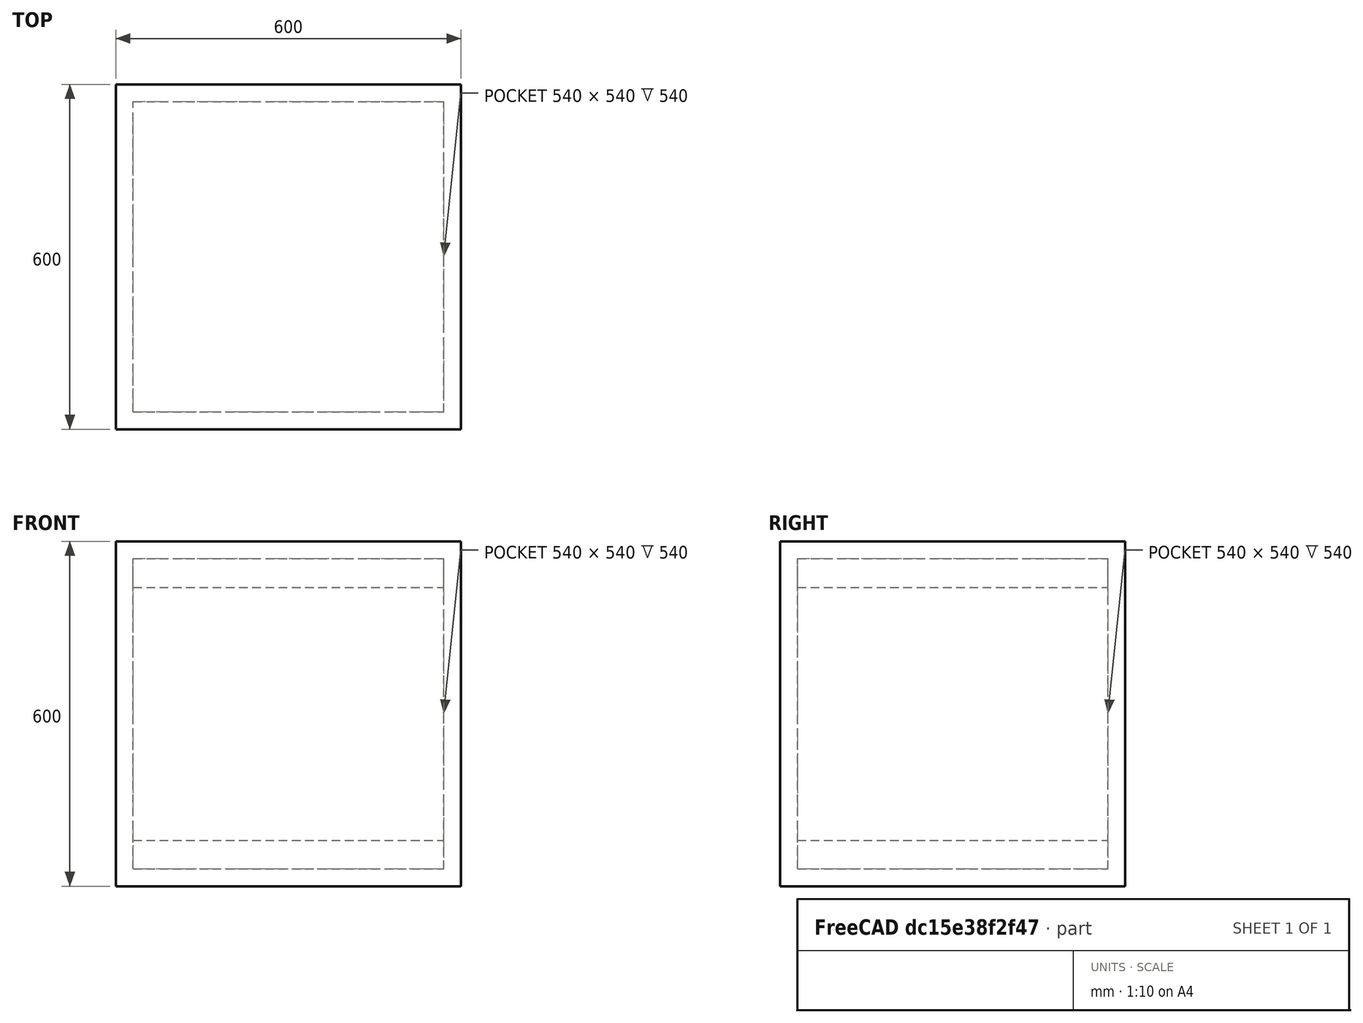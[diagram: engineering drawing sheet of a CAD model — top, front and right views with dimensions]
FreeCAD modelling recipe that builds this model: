
FCSTD DOCUMENT  (FreeCAD 0.17R13541 (Git))
Label: Box_komplett
License: All rights reserved
LicenseURL: http://en.wikipedia.org/wiki/All_rights_reserved
objects: Part::Box×4, Part::Cut×1
note: 5 computed .brp shape members not serialized (recipe doc carries the construction recipe); baked Part::Feature solids carry a one-line shape summary decoded from their .brp

FEATURE [Part::Box] Box  label="Würfel"
  AttacherType = Attacher::AttachEngine3D
  Height = 600
  Length = 600
  Width = 600
FEATURE [Part::Box] Box001  label="Loch"
  AttacherType = Attacher::AttachEngine3D
  Height = 540
  Length = 540
  Placement = pos=(30,30,30) rot=(0,0,1;0rad)
  Width = 540
FEATURE [Part::Cut] Cut
  Base = -> Box
  Tool = -> Box001
FEATURE [Part::Box] Box002  label="Akku_bot"
  AttacherType = Attacher::AttachEngine3D
  Height = 50
  Length = 540
  Placement = pos=(30,30,30) rot=(0,0,1;0rad)
  Width = 540
FEATURE [Part::Box] Box003  label="Akku_top"
  AttacherType = Attacher::AttachEngine3D
  Height = 50
  Length = 540
  Placement = pos=(30,30,520) rot=(0,0,1;0rad)
  Width = 540
